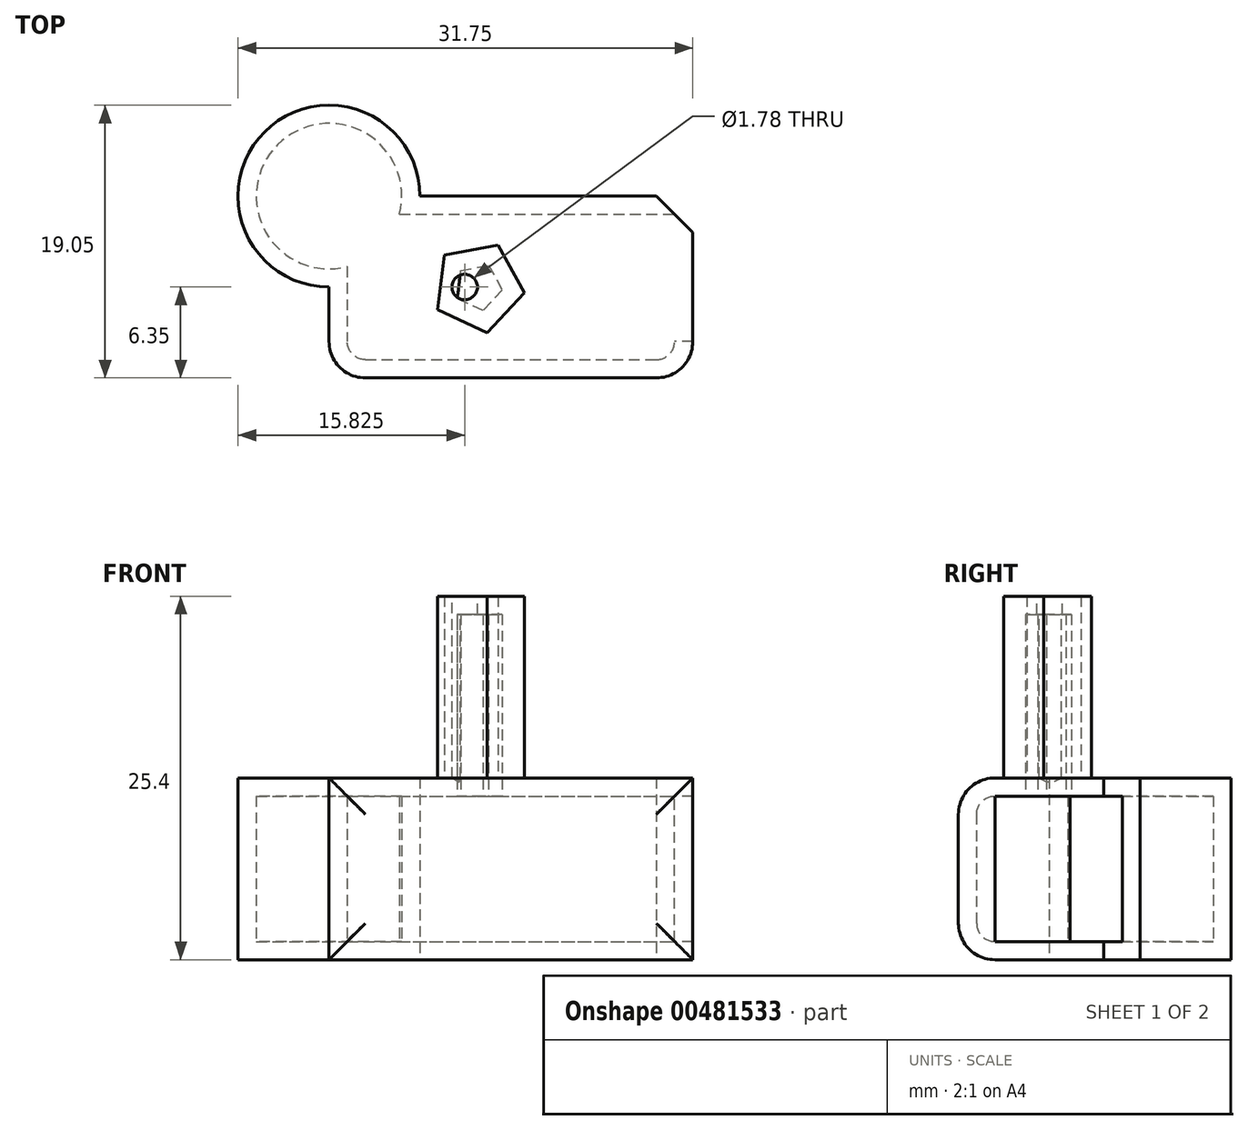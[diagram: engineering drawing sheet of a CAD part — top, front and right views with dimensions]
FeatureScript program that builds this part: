
annotation { "Feature Type Name" : "Feature", "Feature Type Description" : "" }
export const myFeature = defineFeature(function(context is Context, id is Id, definition is map)
    precondition{}
    {
        {
            var Q0;
            Q0=qCreatedBy(makeId("Top.planeOp"),FACE);
            var sketch = newSketch(context, id + "F0", { "sketchPlane" : qUnion([Q0])});
            skLineSegment(sketch, "E0.bottom", {"start": v(-12.7, 6.35) * mm, "end": v(12.7, 6.35) * mm});
            skLineSegment(sketch, "E0.top", {"start": v(-12.7, -6.35) * mm, "end": v(12.7, -6.35) * mm});
            skLineSegment(sketch, "E0.left", {"start": v(-12.7, 6.35) * mm, "end": v(-12.7, -6.35) * mm});
            skLineSegment(sketch, "E0.right", {"start": v(12.7, 6.35) * mm, "end": v(12.7, -6.35) * mm});
            skPoint(sketch, "E0.middle", {"position": v(0, 0) * mm});
            skCircle(sketch, "E1", {"center": v(-12.7, 6.35) * mm, "radius": 6.35 * mm});
            skSolve(sketch);
        }
        {
            var Q0;
            Q0 = qSketchRegion(id + "F0", true);
            extrude(context, id + "F1", {"entities" : qUnion([Q0]), "endBound" : BoundingType.SYMMETRIC, "depth" : 12.7 * mm});
        }
        {
            var Q0;
            Q0=makeQuery(id+"F1.opExtrude","CAP_FACE",FACE,{"disambiguationData":[OSD([sQuery(id+"F0.wireOp",EDGE,"E0.bottom"),sQuery(id+"F0.wireOp",EDGE,"E0.top"),sQuery(id+"F0.wireOp",EDGE,"E0.left"),sQuery(id+"F0.wireOp",EDGE,"E0.right"),sQuery(id+"F0.wireOp",EDGE,"E1")])],"isStart":false});
            var sketch = newSketch(context, id + "F2", { "sketchPlane" : qUnion([Q0])});
            skCircle(sketch, "E2.cCircle", {"center": v(-2.27, 0) * mm, "radius": 2.63 * mm, "construction": true});
            skLineSegment(sketch, "E2.0", {"start": v(0.96, -0.4) * mm, "end": v(-1.66, -3.2) * mm});
            skLineSegment(sketch, "E2.1", {"start": v(-1.66, -3.2) * mm, "end": v(-5.12, -1.57) * mm});
            skLineSegment(sketch, "E2.2", {"start": v(-5.12, -1.57) * mm, "end": v(-4.65, 2.22) * mm});
            skLineSegment(sketch, "E2.3", {"start": v(-4.65, 2.22) * mm, "end": v(-0.89, 2.95) * mm});
            skLineSegment(sketch, "E2.4", {"start": v(-0.89, 2.95) * mm, "end": v(0.96, -0.4) * mm});
            skPoint(sketch, "E2.0.midPoint", {"position": v(-0.35, -1.8) * mm});
            skSolve(sketch);
        }
        {
            var Q0;
            Q0 = qSketchRegion(id + "F2", true);
            var Q1;
            Q1=makeQuery(id+"F1.opExtrude","CAP_FACE",FACE,{"disambiguationData":[OSD([sQuery(id+"F0.wireOp",EDGE,"E0.bottom"),sQuery(id+"F0.wireOp",EDGE,"E0.top"),sQuery(id+"F0.wireOp",EDGE,"E0.left"),sQuery(id+"F0.wireOp",EDGE,"E0.right"),sQuery(id+"F0.wireOp",EDGE,"E1")])],"isStart":false});
            extrude(context, id + "F3", {"entities" : qUnion([Q0]), "operationType" : NewBodyOperationType.ADD, "endBoundEntityFace" : qUnion([Q1]), "depth" : 12.7 * mm});
        }
        {
            var Q0;
            Q0=makeQuery(id+"F1.opExtrude","SWEPT_FACE",FACE,{"disambiguationData":[OSD([sQuery(id+"F0.wireOp",EDGE,"E0.top")])]});
            fillet(context, id + "F4", {"entities" : qUnion([Q0]), "radius" : 2.54 * mm, "allowEdgeOverflow" : false});
        }
        {
            var Q0;
            Q0=makeQuery(id+"F1.opExtrude","SWEPT_FACE",FACE,{"disambiguationData":[OSD([sQuery(id+"F0.wireOp",EDGE,"E0.right")])]});
            shell(context, id + "F5", {"entities" : qUnion([Q0]), "thickness" : 1.27 * mm});
        }
        {
            var Q0;
            Q0=makeQuery(id+"F1.opExtrude","SWEPT_EDGE",EDGE,{"disambiguationData":[OSD([sQuery(id+"F0.wireOp",EDGE,"E0.bottom"),sQuery(id+"F0.wireOp",EDGE,"E0.right")])]});
            chamfer(context, id + "F6", {"entities" : qUnion([Q0]), "width" : 2.54 * mm, "tangentPropagation" : true});
        }
        {
            var Q0;
            Q0=makeQuery(id+"F3.opExtrude","CAP_FACE",FACE,{"disambiguationData":[OSD([sQuery(id+"F2.wireOp",EDGE,"E2.0"),sQuery(id+"F2.wireOp",EDGE,"E2.1"),sQuery(id+"F2.wireOp",EDGE,"E2.2"),sQuery(id+"F2.wireOp",EDGE,"E2.3"),sQuery(id+"F2.wireOp",EDGE,"E2.4")])],"isStart":false});
            var sketch = newSketch(context, id + "F7", { "sketchPlane" : qUnion([Q0])});
            skCircle(sketch, "E3", {"center": v(-3.22, 0) * mm, "radius": 1.37 * mm});
            skSolve(sketch);
        }
        {
            var Q0;
            Q0=sQuery(id+"F7.wireOp",VERTEX,"E3.center");
            var Q1;
            Q1=makeQuery(id+"F1.opExtrude","SWEPT_BODY",BODY,{"disambiguationData":[OSD([sQuery(id+"F0.wireOp",EDGE,"E0.bottom"),sQuery(id+"F0.wireOp",EDGE,"E0.top"),sQuery(id+"F0.wireOp",EDGE,"E0.left"),sQuery(id+"F0.wireOp",EDGE,"E0.right"),sQuery(id+"F0.wireOp",EDGE,"E1")])]});
            hole(context, id + "F8", {"style" : HoleStyle.SIMPLE, "endStyle" : HoleEndStyle.BLIND, "holeDiameter" : 1.78 * mm, "holeDepth" : 12.7 * mm, "isTappedThrough" : true, "tappedDepth" : 12.7 * mm, "tapClearance" : 3, "locations" : qUnion([Q0]), "scope" : qUnion([Q1])});
        }
    });
